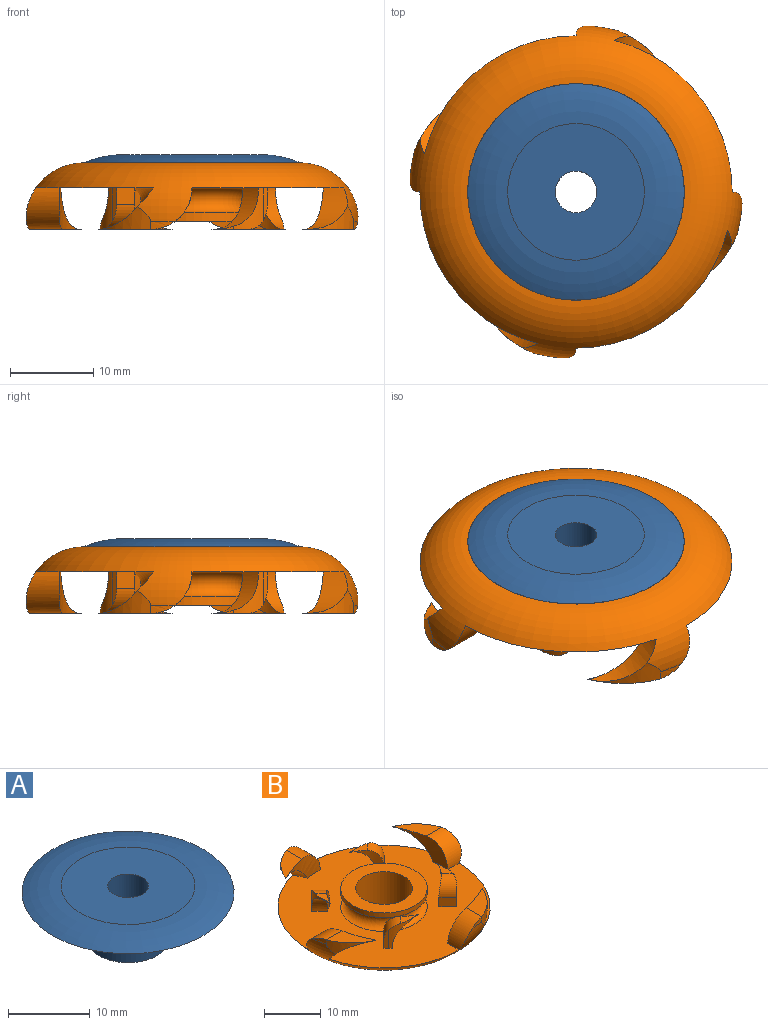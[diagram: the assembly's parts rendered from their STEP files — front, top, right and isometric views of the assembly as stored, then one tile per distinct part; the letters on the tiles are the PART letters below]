
ASSEMBLY  parts=2 mates=1
PART A: 6 faces, bbox 26x26x8 mm
  f0: cylinder r=2.5mm len=8mm, axis (0,0,-1), area 125.7mm2, adj f1,f4
  f1: plane 16.41x16.41mm, normal (0,0,1), area 191.8mm2, adj f0,f5
  f2: plane 26x26mm, normal (0,0,-1), area 452.4mm2, adj f3,f5
  f3: cylinder r=5mm len=10mm, axis (0,0,1), area 219.9mm2, adj f2,f4
  f4: plane 10x10mm, normal (0,0,-1), area 58.9mm2, adj f0,f3
  f5: torus R=8.2mm, axis (0,0,-1), area 329.7mm2, adj f1,f2
PART B: 67 faces, bbox 43.3x43.3x12 mm
  f0: plane 37.49x37.49mm, normal (0,0,1), area 859.2mm2, adj f2,f3,f7,f8,f11,f12,f13,f16
  f1: plane 6.23x6.1mm, normal (0,0,1), area 16.6mm2, adj f5,f7,f8,f10
  f2: cylinder r=9.1mm len=9.03mm, axis (-0.43,0.9,0), area 24.5mm2, adj f0,f3,f5,f7,f10
  f3: torus R=13mm, axis (0,0,1), area 768.2mm2, adj f0,f2,f4,f6,f8,f10,f21,f23
  f4: plane 26x26mm, normal (0,0,-1), area 452.4mm2, adj f3,f9
  f5: plane 1.22x0.58mm, normal (-0.43,0.9,0), area 0mm2, adj f1,f2,f7
  f6: cylinder r=20mm len=3mm, axis (0,0,-1), area 2.1mm2, adj f3,f8,f10
  f7: cylinder r=21.69mm len=10.01mm, axis (0,0,1), area 23.7mm2, adj f0,f1,f2,f5,f8
  f8: cylinder r=5mm len=5mm, axis (0,1,0), area 29.8mm2, adj f0,f1,f3,f6,f7
  f9: cylinder r=5mm len=10mm, axis (0,0,-1), area 219.9mm2, adj f4,f66
  f10: cylinder r=10.46mm len=6.23mm, axis (0,0,1), area 9.4mm2, adj f1,f2,f3,f6
  f11: torus R=7.64mm, axis (0,0,-1), area 197.9mm2, adj f0,f65
  f12: plane 2.19x2.19mm, normal (-0.71,-0.71,0), area 6.2mm2, adj f0,f13,f17,f19
  f13: plane 3.94x0.5mm, normal (0.71,-0.71,0), area 2.4mm2, adj f0,f12,f17,f18
  f14: plane 2.62x0.41mm, normal (1,0.01,0), area 0.3mm2, adj f15,f16,f18
  f15: plane 4.13x1.73mm, normal (0,0,1), area 3.3mm2, adj f14,f17,f18,f19
  f16: cylinder r=4.6mm len=5.56mm, axis (-0.71,0.71,0), area 14.6mm2, adj f0,f14,f18,f19
  f17: cylinder r=3mm len=4.31mm, axis (-0.71,0.71,0), area 13.1mm2, adj f12,f13,f15,f18,f19
  f18: cylinder r=5mm len=5mm, axis (0,0,-1), area 7.8mm2, adj f0,f13,f14,f15,f16,f17
  f19: cylinder r=8.96mm len=5mm, axis (0,0,1), area 10.2mm2, adj f0,f12,f15,f16,f17
  f20: plane 6.23x6.1mm, normal (0,0,1), area 16.6mm2, adj f22,f24,f25,f26
  f21: cylinder r=9.1mm len=9.03mm, axis (0.9,0.43,0), area 24.5mm2, adj f0,f3,f22,f24,f26
  f22: plane 1.22x0.58mm, normal (0.9,0.43,0), area 0mm2, adj f20,f21,f24
  f23: cylinder r=20mm len=3mm, axis (0,0,-1), area 2.1mm2, adj f3,f25,f26
  f24: cylinder r=21.69mm len=10.01mm, axis (0,0,1), area 23.7mm2, adj f0,f20,f21,f22,f25
  f25: cylinder r=5mm len=5mm, axis (1,0,0), area 29.8mm2, adj f0,f3,f20,f23,f24
  f26: cylinder r=10.46mm len=6.23mm, axis (0,0,1), area 9.4mm2, adj f3,f20,f21,f23
  f27: plane 2.19x2.19mm, normal (-0.71,0.71,0), area 6.2mm2, adj f0,f28,f32,f34
  f28: plane 3.94x0.5mm, normal (-0.71,-0.71,0), area 2.4mm2, adj f0,f27,f32,f33
  f29: plane 2.62x0.41mm, normal (0.01,-1,0), area 0.3mm2, adj f30,f31,f33
  f30: plane 4.13x1.73mm, normal (0,0,1), area 3.3mm2, adj f29,f32,f33,f34
  f31: cylinder r=4.6mm len=5.56mm, axis (0.71,0.71,0), area 14.6mm2, adj f0,f29,f33,f34
  f32: cylinder r=3mm len=4.31mm, axis (0.71,0.71,0), area 13.1mm2, adj f27,f28,f30,f33,f34
  f33: cylinder r=5mm len=5mm, axis (0,0,-1), area 7.8mm2, adj f0,f28,f29,f30,f31,f32
  f34: cylinder r=8.96mm len=5mm, axis (0,0,1), area 10.2mm2, adj f0,f27,f30,f31,f32
  f35: plane 6.23x6.1mm, normal (0,0,1), area 16.6mm2, adj f37,f39,f40,f41
  f36: cylinder r=9.1mm len=9.03mm, axis (0.43,-0.9,0), area 24.5mm2, adj f0,f3,f37,f39,f41
  f37: plane 1.22x0.58mm, normal (0.43,-0.9,0), area 0mm2, adj f35,f36,f39
  f38: cylinder r=20mm len=3mm, axis (0,0,-1), area 2.1mm2, adj f3,f40,f41
  f39: cylinder r=21.69mm len=10.01mm, axis (0,0,1), area 23.7mm2, adj f0,f35,f36,f37,f40
  f40: cylinder r=5mm len=5mm, axis (0,-1,0), area 29.8mm2, adj f0,f3,f35,f38,f39
  f41: cylinder r=10.46mm len=6.23mm, axis (0,0,1), area 9.4mm2, adj f3,f35,f36,f38
  f42: plane 2.19x2.19mm, normal (0.71,0.71,0), area 6.2mm2, adj f0,f43,f47,f49
  f43: plane 3.94x0.5mm, normal (-0.71,0.71,0), area 2.4mm2, adj f0,f42,f47,f48
  f44: plane 2.62x0.41mm, normal (-1,-0.01,0), area 0.3mm2, adj f45,f46,f48
  f45: plane 4.13x1.73mm, normal (0,0,1), area 3.3mm2, adj f44,f47,f48,f49
  f46: cylinder r=4.6mm len=5.56mm, axis (0.71,-0.71,0), area 14.6mm2, adj f0,f44,f48,f49
  f47: cylinder r=3mm len=4.31mm, axis (0.71,-0.71,0), area 13.1mm2, adj f42,f43,f45,f48,f49
  f48: cylinder r=5mm len=5mm, axis (0,0,-1), area 7.8mm2, adj f0,f43,f44,f45,f46,f47
  f49: cylinder r=8.96mm len=5mm, axis (0,0,1), area 10.2mm2, adj f0,f42,f45,f46,f47
  f50: plane 6.23x6.1mm, normal (0,0,1), area 16.6mm2, adj f52,f54,f55,f56
  f51: cylinder r=9.1mm len=9.03mm, axis (-0.9,-0.43,0), area 24.5mm2, adj f0,f3,f52,f54,f56
  f52: plane 1.22x0.58mm, normal (-0.9,-0.43,0), area 0mm2, adj f50,f51,f54
  f53: cylinder r=20mm len=3mm, axis (0,0,-1), area 2.1mm2, adj f3,f55,f56
  f54: cylinder r=21.69mm len=10.01mm, axis (0,0,1), area 23.7mm2, adj f0,f50,f51,f52,f55
  f55: cylinder r=5mm len=5mm, axis (-1,0,0), area 29.8mm2, adj f0,f3,f50,f53,f54
  f56: cylinder r=10.46mm len=6.23mm, axis (0,0,1), area 9.4mm2, adj f3,f50,f51,f53
  f57: plane 2.19x2.19mm, normal (0.71,-0.71,0), area 6.2mm2, adj f0,f58,f62,f64
  f58: plane 3.94x0.5mm, normal (0.71,0.71,0), area 2.4mm2, adj f0,f57,f62,f63
  f59: plane 2.62x0.41mm, normal (-0.01,1,0), area 0.3mm2, adj f60,f61,f63
  f60: plane 4.13x1.73mm, normal (0,0,1), area 3.3mm2, adj f59,f62,f63,f64
  f61: cylinder r=4.6mm len=5.56mm, axis (-0.71,-0.71,0), area 14.6mm2, adj f0,f59,f63,f64
  f62: cylinder r=3mm len=4.31mm, axis (-0.71,-0.71,0), area 13.1mm2, adj f57,f58,f60,f63,f64
  f63: cylinder r=5mm len=5mm, axis (0,0,-1), area 7.8mm2, adj f0,f58,f59,f60,f61,f62
  f64: cylinder r=8.96mm len=5mm, axis (0,0,1), area 10.2mm2, adj f0,f57,f60,f61,f62
  f65: cylinder r=7.64mm len=15.28mm, axis (0,0,-1), area 48mm2, adj f11,f66
  f66: plane 15.28x15.28mm, normal (0,0,1), area 104.9mm2, adj f9,f65
PLACE A t=(-16.31,-9.77,7.25)mm
PLACE B rot(axis=(0,1,0),180deg) t=(-16.31,-9.77,7.25)mm
MATE fastened A.f0 <-> B.f9  axis (0,0,-1) through (-16.31,-9.77,0.25)mm
